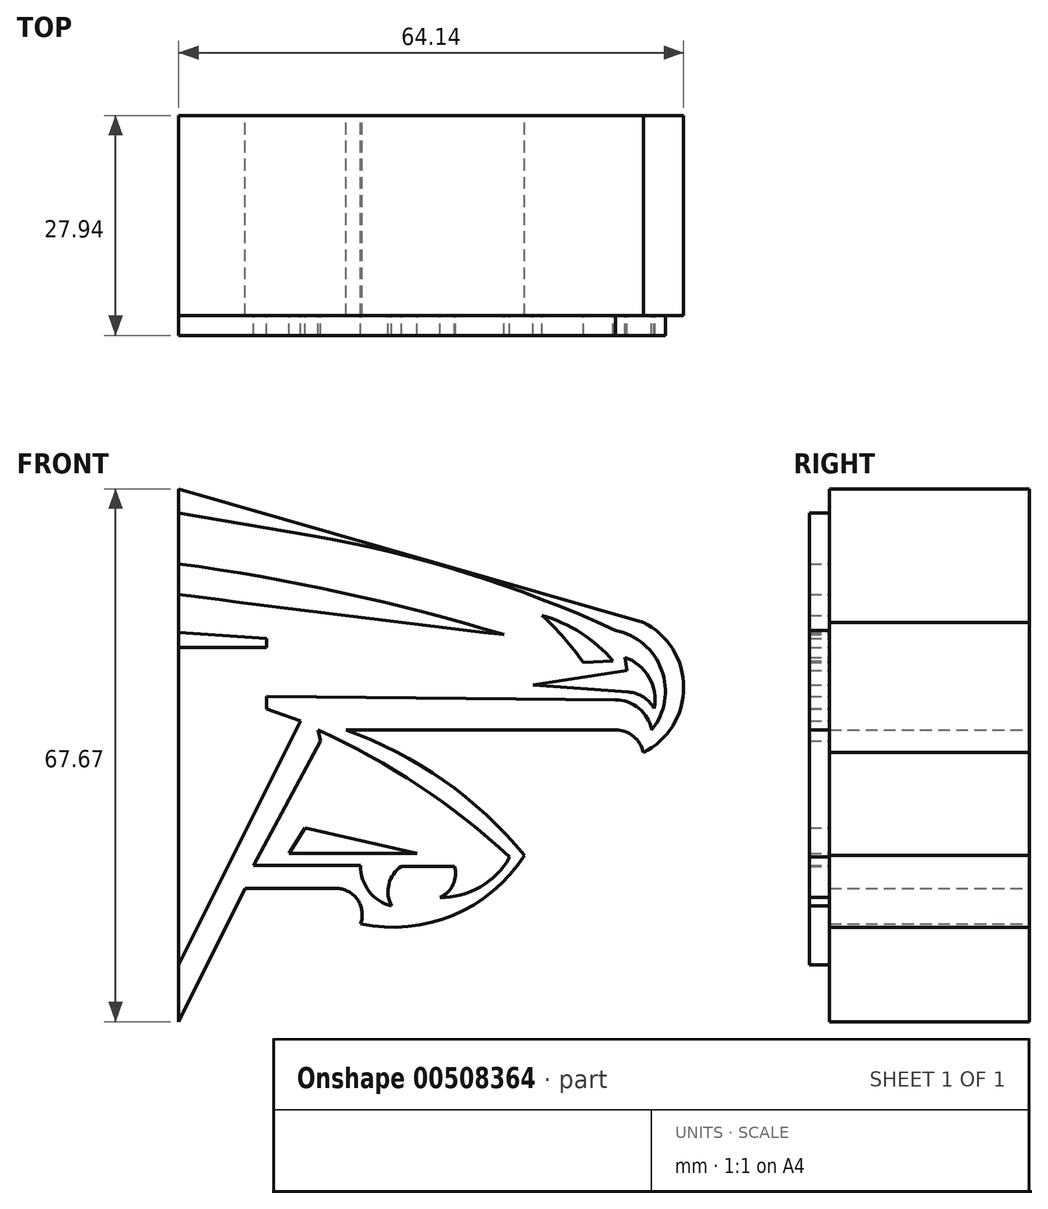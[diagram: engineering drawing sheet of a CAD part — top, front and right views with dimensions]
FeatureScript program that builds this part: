
annotation { "Feature Type Name" : "Feature", "Feature Type Description" : "" }
export const myFeature = defineFeature(function(context is Context, id is Id, definition is map)
    precondition{}
    {
        {
            var Q0;
            Q0=qCreatedBy(makeId("Front.planeOp"),FACE);
            var sketch = newSketch(context, id + "F0", { "sketchPlane" : qUnion([Q0])});
            skLineSegment(sketch, "E0", {"start": v(4.68, -29.02) * mm, "end": v(13.14, -12.09) * mm});
            skLineSegment(sketch, "E1", {"start": v(13.14, -12.09) * mm, "end": v(24.64, -12.09) * mm});
            skArc(sketch, "E2", {"start": v(27.79, -16.59) * mm, "mid": v(27.4, -13.52) * mm, "end": v(24.64, -12.09) * mm});
            skArc(sketch, "E3", {"start": v(27.79, -16.59) * mm, "mid": v(39.53, -15.5) * mm, "end": v(48.58, -7.92) * mm});
            skArc(sketch, "E4", {"start": v(48.58, -7.92) * mm, "mid": v(38.34, 1.63) * mm, "end": v(25.9, 8.04) * mm});
            skLineSegment(sketch, "E5", {"start": v(25.9, 8.04) * mm, "end": v(60.16, 8.04) * mm});
            skArc(sketch, "E6", {"start": v(63.7, 5.17) * mm, "mid": v(62.44, 7.23) * mm, "end": v(60.16, 8.04) * mm});
            skArc(sketch, "E7", {"start": v(63.7, 5.17) * mm, "mid": v(68.82, 13.44) * mm, "end": v(63.7, 21.7) * mm});
            skLineSegment(sketch, "E8", {"start": v(63.7, 21.7) * mm, "end": v(4.68, 38.65) * mm});
            skLineSegment(sketch, "E9", {"start": v(4.68, 38.65) * mm, "end": v(4.68, -29.02) * mm});
            skPoint(sketch, "E10.end.orphan", {"position": v(-8, -68.44) * mm});
            skPoint(sketch, "E11.orphan", {"position": v(-8, -54.41) * mm});
            skSolve(sketch);
        }
        {
            var Q0;
            Q0 = qSketchRegion(id + "F0", true);
            extrude(context, id + "F1", {"entities" : qUnion([Q0]), "depth" : 25.4 * mm});
        }
        {
            var Q0;
            Q0=makeQuery(id+"F1.opExtrude","CAP_FACE",FACE,{"disambiguationData":[OSD([sQuery(id+"F0.wireOp",EDGE,"E0"),sQuery(id+"F0.wireOp",EDGE,"E1"),sQuery(id+"F0.wireOp",EDGE,"E2"),sQuery(id+"F0.wireOp",EDGE,"E3"),sQuery(id+"F0.wireOp",EDGE,"E4"),sQuery(id+"F0.wireOp",EDGE,"E5"),sQuery(id+"F0.wireOp",EDGE,"E6"),sQuery(id+"F0.wireOp",EDGE,"E7"),sQuery(id+"F0.wireOp",EDGE,"E8"),sQuery(id+"F0.wireOp",EDGE,"E9")])],"isStart":false});
            var sketch = newSketch(context, id + "F2", { "sketchPlane" : qUnion([Q0])});
            skArc(sketch, "E12", {"start": v(56.07, 16.59) * mm, "mid": v(53.62, 19.74) * mm, "end": v(50.82, 22.6) * mm});
            skArc(sketch, "E13", {"start": v(59.87, 16.8) * mm, "mid": v(55.77, 20.36) * mm, "end": v(50.82, 22.6) * mm});
            skLineSegment(sketch, "E14", {"start": v(56.07, 16.59) * mm, "end": v(59.87, 16.8) * mm});
            skLineSegment(sketch, "E15", {"start": v(49.71, 13.76) * mm, "end": v(61.6, 15.6) * mm});
            skLineSegment(sketch, "E16", {"start": v(49.71, 13.76) * mm, "end": v(61.8, 12.84) * mm});
            skArc(sketch, "E17", {"start": v(65.08, 10.8) * mm, "mid": v(63.7, 12.22) * mm, "end": v(61.8, 12.84) * mm});
            skLineSegment(sketch, "E18", {"start": v(61.6, 15.6) * mm, "end": v(61.34, 17.26) * mm});
            skArc(sketch, "E19", {"start": v(65.08, 10.8) * mm, "mid": v(64.42, 14.73) * mm, "end": v(61.34, 17.26) * mm});
            skArc(sketch, "E20", {"start": v(46, 20.14) * mm, "mid": v(25.52, 25.45) * mm, "end": v(4.68, 29.15) * mm});
            skArc(sketch, "E21", {"start": v(4.68, 25.27) * mm, "mid": v(25.33, 22.62) * mm, "end": v(46, 20.14) * mm});
            skLineSegment(sketch, "E22", {"start": v(20.7, -4.39) * mm, "end": v(18.68, -7.65) * mm});
            skLineSegment(sketch, "E23", {"start": v(18.68, -7.65) * mm, "end": v(34.98, -7.65) * mm});
            skLineSegment(sketch, "E24", {"start": v(34.98, -7.65) * mm, "end": v(20.7, -4.39) * mm});
            skLineSegment(sketch, "E25", {"start": v(22.72, 6.64) * mm, "end": v(14.18, -9.2) * mm});
            skLineSegment(sketch, "E26", {"start": v(14.18, -9.2) * mm, "end": v(27.79, -9.2) * mm});
            skArc(sketch, "E27", {"start": v(27.79, -9.2) * mm, "mid": v(28.86, -12.45) * mm, "end": v(31.72, -14.32) * mm});
            skArc(sketch, "E28", {"start": v(32.98, -9.28) * mm, "mid": v(31.38, -11.56) * mm, "end": v(31.72, -14.32) * mm});
            skLineSegment(sketch, "E29", {"start": v(32.98, -9.28) * mm, "end": v(39.7, -9.28) * mm});
            skArc(sketch, "E30", {"start": v(37.87, -13.23) * mm, "mid": v(39.55, -11.61) * mm, "end": v(39.7, -9.28) * mm});
            skArc(sketch, "E31", {"start": v(37.87, -13.23) * mm, "mid": v(43, -11.9) * mm, "end": v(46.72, -8.12) * mm});
            skArc(sketch, "E32", {"start": v(46.72, -8.12) * mm, "mid": v(35.21, 0.95) * mm, "end": v(22.39, 8.04) * mm});
            skLineSegment(sketch, "E33", {"start": v(22.39, 8.04) * mm, "end": v(22.72, 6.64) * mm});
            skLineSegment(sketch, "E34", {"start": v(4.68, 18.55) * mm, "end": v(15.81, 18.55) * mm});
            skLineSegment(sketch, "E35", {"start": v(15.81, 18.55) * mm, "end": v(15.81, 19.64) * mm});
            skLineSegment(sketch, "E36", {"start": v(15.81, 19.64) * mm, "end": v(4.68, 20.41) * mm});
            skLineSegment(sketch, "E37", {"start": v(4.68, -21.82) * mm, "end": v(20.17, 9.2) * mm});
            skLineSegment(sketch, "E38", {"start": v(20.17, 9.2) * mm, "end": v(15.81, 10.7) * mm});
            skLineSegment(sketch, "E39", {"start": v(15.81, 10.7) * mm, "end": v(15.81, 12.32) * mm});
            skLineSegment(sketch, "E40", {"start": v(15.81, 12.32) * mm, "end": v(60.16, 11.88) * mm});
            skArc(sketch, "E41", {"start": v(64.77, 8.04) * mm, "mid": v(63.15, 10.78) * mm, "end": v(60.16, 11.88) * mm});
            skArc(sketch, "E42", {"start": v(64.77, 8.04) * mm, "mid": v(66.03, 15.66) * mm, "end": v(60.16, 20.68) * mm});
            skArc(sketch, "E43", {"start": v(60.16, 20.68) * mm, "mid": v(41.2, 27.98) * mm, "end": v(21.44, 32.73) * mm});
            skLineSegment(sketch, "E44", {"start": v(21.44, 32.73) * mm, "end": v(4.68, 35.61) * mm});
            skLineSegment(sketch, "E45", {"start": v(4.68, 35.61) * mm, "end": v(4.68, 29.15) * mm});
            skLineSegment(sketch, "E46", {"start": v(4.68, 25.27) * mm, "end": v(4.68, 20.41) * mm});
            skLineSegment(sketch, "E47", {"start": v(4.68, 18.55) * mm, "end": v(4.68, -21.82) * mm});
            skSolve(sketch);
        }
        {
            var Q0;
            Q0 = qSketchRegion(id + "F2", true);
            extrude(context, id + "F3", {"entities" : qUnion([Q0]), "operationType" : NewBodyOperationType.ADD, "depth" : 2.54 * mm});
        }
    });
